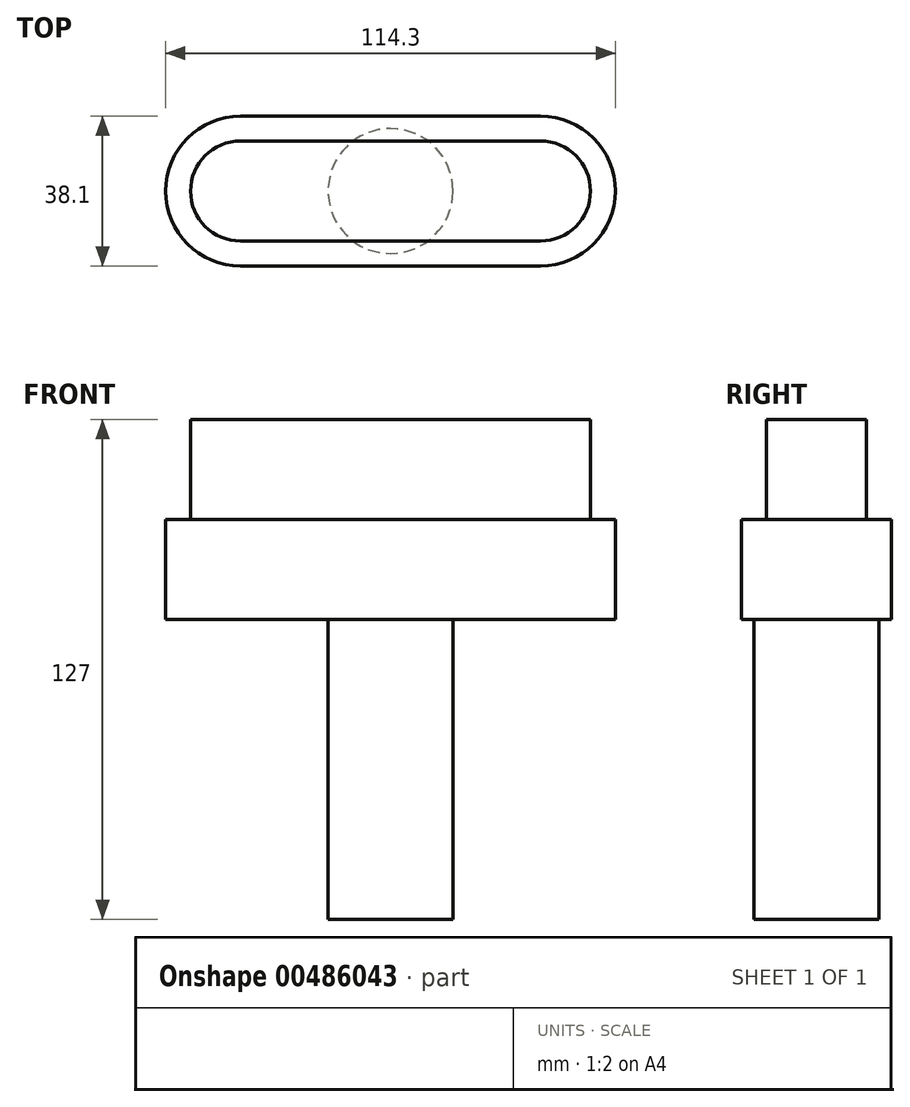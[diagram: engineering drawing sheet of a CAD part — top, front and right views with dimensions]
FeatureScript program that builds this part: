
annotation { "Feature Type Name" : "Feature", "Feature Type Description" : "" }
export const myFeature = defineFeature(function(context is Context, id is Id, definition is map)
    precondition{}
    {
        {
            var Q0;
            Q0=qCreatedBy(makeId("Top.planeOp"),FACE);
            var sketch = newSketch(context, id + "F0", { "sketchPlane" : qUnion([Q0])});
            skArc(sketch, "E0", {"start": v(0, 19.05) * mm, "mid": v(-19.05, 0) * mm, "end": v(0, -19.05) * mm});
            skLineSegment(sketch, "E1", {"start": v(0, 19.05) * mm, "end": v(76.2, 19.05) * mm});
            skLineSegment(sketch, "E2", {"start": v(0, -19.05) * mm, "end": v(76.2, -19.05) * mm});
            skArc(sketch, "E3", {"start": v(76.2, -19.05) * mm, "mid": v(95.25, 0) * mm, "end": v(76.2, 19.05) * mm});
            skSolve(sketch);
        }
        {
            var Q0;
            Q0=makeQuery(id+"F0.imprint","IMPRINT",FACE,{"disambiguationData":[TD([[makeQuery(id+"F0.imprint","IMPRINT",EDGE,{"derivedFrom":sQuery(id+"F0.wireOp",EDGE,"E0")}),1.0]])]});
            extrude(context, id + "F1", {"entities" : qUnion([Q0]), "depth" : 25.4 * mm});
        }
        {
            var Q0;
            Q0=makeQuery(id+"F1.opExtrude","CAP_FACE",FACE,{"disambiguationData":[OSD([sQuery(id+"F0.wireOp",EDGE,"E0"),sQuery(id+"F0.wireOp",EDGE,"E1"),sQuery(id+"F0.wireOp",EDGE,"E2"),sQuery(id+"F0.wireOp",EDGE,"E3")])],"isStart":false});
            var sketch = newSketch(context, id + "F2", { "sketchPlane" : qUnion([Q0])});
            skArc(sketch, "E4", {"start": v(0, 12.7) * mm, "mid": v(-12.7, 0) * mm, "end": v(0, -12.7) * mm});
            skCircle(sketch, "E5", {"center": v(76.2, 0) * mm, "radius": 12.7 * mm});
            skLineSegment(sketch, "E6", {"start": v(0, -12.7) * mm, "end": v(76.2, -12.7) * mm});
            skLineSegment(sketch, "E7", {"start": v(76.2, 12.7) * mm, "end": v(0, 12.7) * mm});
            skSolve(sketch);
        }
        {
            var Q0;
            Q0=makeQuery(id+"F2.imprint","IMPRINT",FACE,{"disambiguationData":[TD([[makeQuery(id+"F2.imprint","IMPRINT",EDGE,{"derivedFrom":sQuery(id+"F2.wireOp",EDGE,"E4")}),1.0]])]});
            var Q1;
            {var subQ0=sQuery(id+"F2.wireOp",EDGE,"E5");var subQ1=makeQuery(id+"F2.imprint","INTERSECT",VERTEX,{"derivedFrom":[subQ0,sQuery(id+"F2.wireOp",EDGE,"E6")]});Q1=makeQuery(id+"F2.imprint","IMPRINT",FACE,{"disambiguationData":[TD([[makeQuery(id+"F2.imprint","IMPRINT",EDGE,{"disambiguationData":[TD([[subQ1,1.0]])],"derivedFrom":subQ0}),1.0]])]});}
            extrude(context, id + "F3", {"entities" : qUnion([Q0, Q1]), "operationType" : NewBodyOperationType.ADD, "depth" : 25.4 * mm});
        }
        {
            var Q0;
            Q0=makeQuery(id+"F1.opExtrude","CAP_FACE",FACE,{"disambiguationData":[OSD([sQuery(id+"F0.wireOp",EDGE,"E0"),sQuery(id+"F0.wireOp",EDGE,"E1"),sQuery(id+"F0.wireOp",EDGE,"E2"),sQuery(id+"F0.wireOp",EDGE,"E3")])],"isStart":true});
            var sketch = newSketch(context, id + "F4", { "sketchPlane" : qUnion([Q0])});
            skCircle(sketch, "E8", {"center": v(38.1, 0) * mm, "radius": 15.88 * mm});
            skPoint(sketch, "E8.centerSnap0", {"position": v(38.1, 19.05) * mm});
            skSolve(sketch);
        }
        {
            var Q0;
            Q0 = qSketchRegion(id + "F4", true);
            extrude(context, id + "F5", {"entities" : qUnion([Q0]), "operationType" : NewBodyOperationType.ADD, "depth" : 76.2 * mm});
        }
    });
